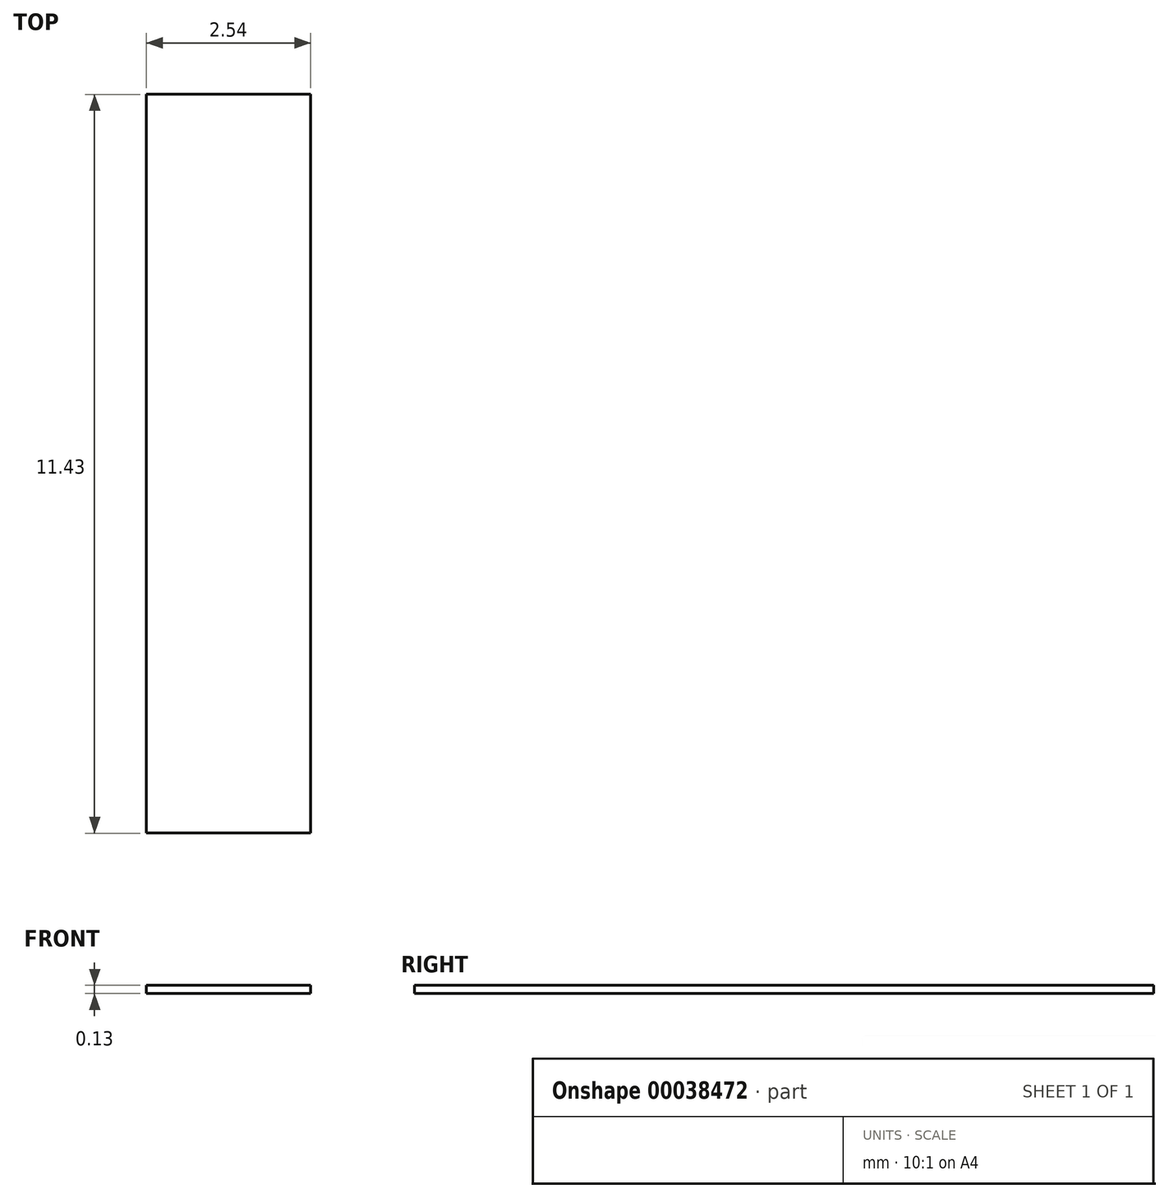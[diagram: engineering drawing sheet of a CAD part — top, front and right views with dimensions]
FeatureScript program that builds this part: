
annotation { "Feature Type Name" : "Feature", "Feature Type Description" : "" }
export const myFeature = defineFeature(function(context is Context, id is Id, definition is map)
    precondition{}
    {
        {
            var Q0;
            Q0=qCreatedBy(makeId("Top.planeOp"),FACE);
            var sketch = newSketch(context, id + "F0", { "sketchPlane" : qUnion([Q0])});
            skLineSegment(sketch, "E0.bottom", {"start": v(-1.44, 2.15) * mm, "end": v(1.1, 2.15) * mm});
            skLineSegment(sketch, "E0.top", {"start": v(-1.44, -1.66) * mm, "end": v(1.1, -1.66) * mm});
            skLineSegment(sketch, "E0.left", {"start": v(-1.44, 2.15) * mm, "end": v(-1.44, -1.66) * mm});
            skLineSegment(sketch, "E0.right", {"start": v(1.1, 2.15) * mm, "end": v(1.1, -1.66) * mm});
            skLineSegment(sketch, "E1.bottom", {"start": v(-1.44, 5.96) * mm, "end": v(1.1, 5.96) * mm});
            skLineSegment(sketch, "E1.left", {"start": v(-1.44, 5.96) * mm, "end": v(-1.44, 2.15) * mm});
            skLineSegment(sketch, "E1.right", {"start": v(1.1, 5.96) * mm, "end": v(1.1, 2.15) * mm});
            skLineSegment(sketch, "E2.top", {"start": v(-1.44, -5.47) * mm, "end": v(1.1, -5.47) * mm});
            skLineSegment(sketch, "E2.left", {"start": v(-1.44, -1.66) * mm, "end": v(-1.44, -5.47) * mm});
            skLineSegment(sketch, "E2.right", {"start": v(1.1, -1.66) * mm, "end": v(1.1, -5.47) * mm});
            skLineSegment(sketch, "E3.bottom", {"start": v(-1.44, 5.96) * mm, "end": v(-0.17, 5.96) * mm});
            skLineSegment(sketch, "E3.top", {"start": v(-1.44, -1.66) * mm, "end": v(-0.17, -1.66) * mm});
            skLineSegment(sketch, "E3.left", {"start": v(-1.44, 5.96) * mm, "end": v(-1.44, -1.66) * mm});
            skLineSegment(sketch, "E3.right", {"start": v(-0.17, 5.96) * mm, "end": v(-0.17, -1.66) * mm});
            skLineSegment(sketch, "E4.left", {"start": v(-0.17, -1.66) * mm, "end": v(-0.17, -1.66) * mm});
            skLineSegment(sketch, "E4.right", {"start": v(3.97, -1.66) * mm, "end": v(3.97, -1.66) * mm});
            skLineSegment(sketch, "E5.bottom", {"start": v(-0.17, -1.66) * mm, "end": v(-1.44, -1.66) * mm});
            skLineSegment(sketch, "E5.top", {"start": v(-0.17, -5.47) * mm, "end": v(-1.44, -5.47) * mm});
            skLineSegment(sketch, "E5.left", {"start": v(-0.17, -1.66) * mm, "end": v(-0.17, -5.47) * mm});
            skLineSegment(sketch, "E6.top", {"start": v(-1.44, 4.06) * mm, "end": v(1.1, 4.06) * mm});
            skLineSegment(sketch, "E6.left", {"start": v(-1.44, 5.96) * mm, "end": v(-1.44, 4.06) * mm});
            skLineSegment(sketch, "E6.right", {"start": v(1.1, 5.96) * mm, "end": v(1.1, 4.06) * mm});
            skLineSegment(sketch, "E7.left", {"start": v(-1.44, 4.06) * mm, "end": v(-1.44, 2.15) * mm});
            skLineSegment(sketch, "E7.right", {"start": v(1.1, 4.06) * mm, "end": v(1.1, 2.15) * mm});
            skLineSegment(sketch, "E8.top", {"start": v(-1.44, 0.25) * mm, "end": v(1.1, 0.25) * mm});
            skLineSegment(sketch, "E8.left", {"start": v(-1.44, 2.15) * mm, "end": v(-1.44, 0.25) * mm});
            skLineSegment(sketch, "E8.right", {"start": v(1.1, 2.15) * mm, "end": v(1.1, 0.25) * mm});
            skLineSegment(sketch, "E9.left", {"start": v(-1.44, 0.25) * mm, "end": v(-1.44, -1.66) * mm});
            skLineSegment(sketch, "E9.right", {"start": v(1.1, 0.25) * mm, "end": v(1.1, -1.66) * mm});
            skLineSegment(sketch, "E10.top", {"start": v(-1.44, -3.56) * mm, "end": v(1.1, -3.56) * mm});
            skLineSegment(sketch, "E10.left", {"start": v(-1.44, -1.66) * mm, "end": v(-1.44, -3.56) * mm});
            skLineSegment(sketch, "E10.right", {"start": v(1.1, -1.66) * mm, "end": v(1.1, -3.56) * mm});
            skLineSegment(sketch, "E11.top", {"start": v(-1.44, 5.01) * mm, "end": v(1.1, 5.01) * mm});
            skLineSegment(sketch, "E11.left", {"start": v(-1.44, 5.96) * mm, "end": v(-1.44, 5.01) * mm});
            skLineSegment(sketch, "E11.right", {"start": v(1.1, 5.96) * mm, "end": v(1.1, 5.01) * mm});
            skLineSegment(sketch, "E12.top", {"start": v(-1.44, 3.1) * mm, "end": v(1.1, 3.1) * mm});
            skLineSegment(sketch, "E12.left", {"start": v(-1.44, 4.06) * mm, "end": v(-1.44, 3.1) * mm});
            skLineSegment(sketch, "E12.right", {"start": v(1.1, 4.06) * mm, "end": v(1.1, 3.1) * mm});
            skLineSegment(sketch, "E13.top", {"start": v(-1.44, 1.2) * mm, "end": v(1.1, 1.2) * mm});
            skLineSegment(sketch, "E13.left", {"start": v(-1.44, 2.15) * mm, "end": v(-1.44, 1.2) * mm});
            skLineSegment(sketch, "E13.right", {"start": v(1.1, 2.15) * mm, "end": v(1.1, 1.2) * mm});
            skLineSegment(sketch, "E14.top", {"start": v(-1.44, -0.7) * mm, "end": v(1.1, -0.7) * mm});
            skLineSegment(sketch, "E14.left", {"start": v(-1.44, 0.25) * mm, "end": v(-1.44, -0.7) * mm});
            skLineSegment(sketch, "E14.right", {"start": v(1.1, 0.25) * mm, "end": v(1.1, -0.7) * mm});
            skLineSegment(sketch, "E15.top", {"start": v(-1.44, -2.6) * mm, "end": v(1.1, -2.6) * mm});
            skLineSegment(sketch, "E15.left", {"start": v(-1.44, -1.66) * mm, "end": v(-1.44, -2.6) * mm});
            skLineSegment(sketch, "E15.right", {"start": v(1.1, -1.66) * mm, "end": v(1.1, -2.6) * mm});
            skLineSegment(sketch, "E16.left", {"start": v(-1.44, -3.56) * mm, "end": v(-1.44, -5.47) * mm});
            skLineSegment(sketch, "E16.right", {"start": v(1.1, -3.56) * mm, "end": v(1.1, -5.47) * mm});
            skLineSegment(sketch, "E17.top", {"start": v(-1.44, -4.51) * mm, "end": v(1.1, -4.51) * mm});
            skLineSegment(sketch, "E17.left", {"start": v(-1.44, -3.56) * mm, "end": v(-1.44, -4.51) * mm});
            skLineSegment(sketch, "E17.right", {"start": v(1.1, -3.56) * mm, "end": v(1.1, -4.51) * mm});
            skLineSegment(sketch, "E18", {"start": v(6.05, 0.88) * mm, "end": v(5.24, 1.6) * mm});
            skSolve(sketch);
        }
        {
            var Q0;
            Q0 = qSketchRegion(id + "F0", true);
            extrude(context, id + "F1", {"entities" : qUnion([Q0]), "depth" : 0.13 * mm});
        }
    });
